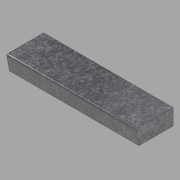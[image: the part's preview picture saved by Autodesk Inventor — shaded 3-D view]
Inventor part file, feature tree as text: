
AUTODESK INVENTOR PART (.ipt)
format: ipt  version: 2022.1 (Build 261234020, 234B)  size: 95,744 bytes
history: native  units: in
note: dims shown in document units (in); Inventor stores cm internally (conversion verified against a paired STEP export)
features: extrude x1, sketch x1
ambient origin geometry x8: Origin, YZ Plane, XZ Plane, XY Plane, X Axis, Y Axis, Z Axis, Center Point
bodies: Solid1 (feature_tree)
feature tree (2):
  extrude  "Extrusion1"  Depth=13.0in
  sketch  "Sketch1"  dims[d0=6.0in d1=13.0in d2=13.5in d3=0.5in d4=49.1953in d5=0.0in]
